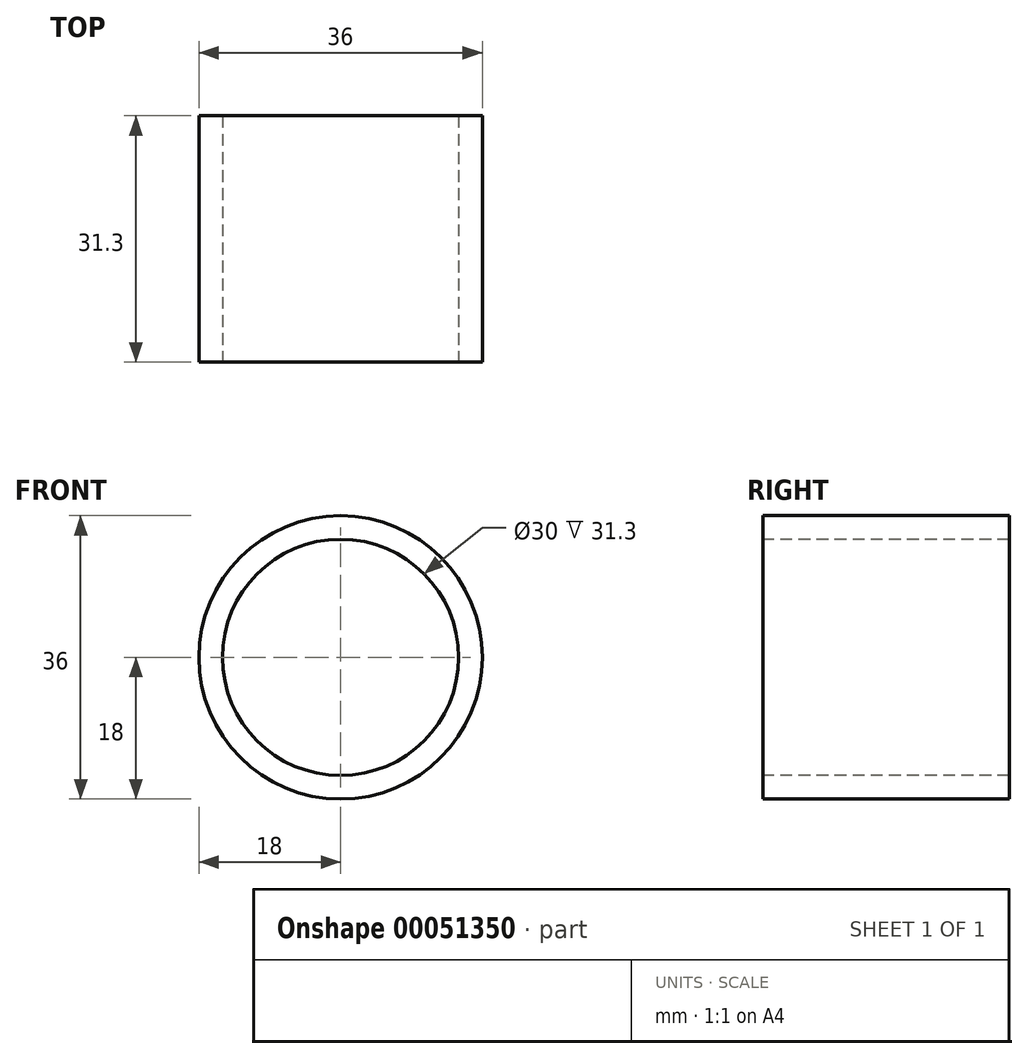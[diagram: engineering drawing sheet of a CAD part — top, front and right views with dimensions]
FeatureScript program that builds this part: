
annotation { "Feature Type Name" : "Feature", "Feature Type Description" : "" }
export const myFeature = defineFeature(function(context is Context, id is Id, definition is map)
    precondition{}
    {
        {
            var Q0;
            Q0=qCreatedBy(makeId("Front.planeOp"),FACE);
            var sketch = newSketch(context, id + "F0", { "sketchPlane" : qUnion([Q0])});
            skCircle(sketch, "E0", {"center": v(0, 0) * mm, "radius": 18 * mm});
            skSolve(sketch);
        }
        {
            var Q0;
            Q0 = qSketchRegion(id + "F0", true);
            extrude(context, id + "F1", {"entities" : qUnion([Q0]), "depth" : (41.8 - 6 - 4.5) * mm, "symmetric" : true});
        }
        {
            var Q0;
            Q0=qCreatedBy(makeId("Front.planeOp"),FACE);
            var sketch = newSketch(context, id + "F2", { "sketchPlane" : qUnion([Q0])});
            skCircle(sketch, "E1", {"center": v(0, 0) * mm, "radius": 15 * mm});
            skSolve(sketch);
        }
        {
            var Q0;
            Q0 = qSketchRegion(id + "F2", true);
            extrude(context, id + "F3", {"entities" : qUnion([Q0]), "operationType" : NewBodyOperationType.REMOVE, "endBound" : BoundingType.THROUGH_ALL, "oppositeDirection" : true, "depth" : 25 * mm, "hasSecondDirection" : true, "secondDirectionBound" : BoundingType.THROUGH_ALL, "secondDirectionOppositeDirection" : false, "secondDirectionDepth" : 25 * mm});
        }
    });
